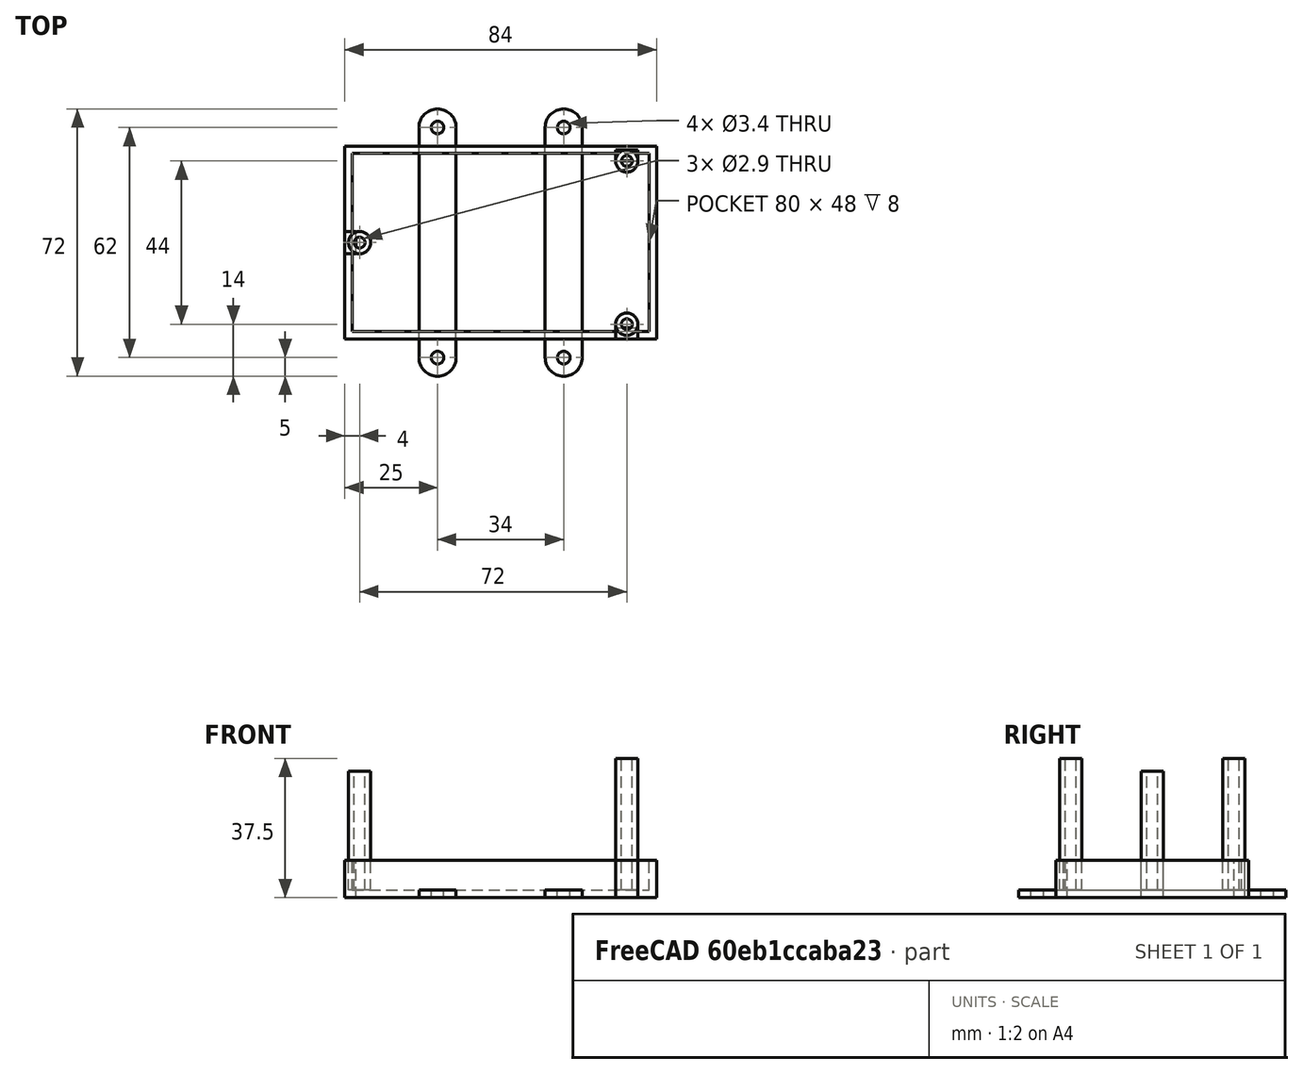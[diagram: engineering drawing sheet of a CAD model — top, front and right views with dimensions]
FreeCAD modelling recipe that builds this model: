
FCSTD DOCUMENT  (FreeCAD 0.18R16093 (Git))
Label: pump_stand
License: All rights reserved
LicenseURL: http://en.wikipedia.org/wiki/All_rights_reserved
objects: Part::Cylinder×14, Part::Box×7, Part::Cut×6, Part::MultiFuse×4, PartDesign::Body×1
note: 32 computed .brp shape members not serialized (recipe doc carries the construction recipe); baked Part::Feature solids carry a one-line shape summary decoded from their .brp

FEATURE [PartDesign::Body] Body
  Origin = -> Origin
FEATURE [Part::Cylinder] Cylinder
  Angle = 360
  AttacherType = Attacher::AttachEngine3D
  Height = 32
  Placement = pos=(4,26,2) rot=(0,0,1;0rad)
  Radius = 3
FEATURE [Part::Box] Box  label="Cube"
  AttacherType = Attacher::AttachEngine3D
  Height = 10
  Length = 84
  Width = 52
FEATURE [Part::Cylinder] Cylinder001
  Angle = 360
  AttacherType = Attacher::AttachEngine3D
  Height = 35.5
  Placement = pos=(76,4,2) rot=(0,0,1;0rad)
  Radius = 3
FEATURE [Part::Cylinder] Cylinder002
  Angle = 360
  AttacherType = Attacher::AttachEngine3D
  Height = 35.5
  Placement = pos=(76,48,2) rot=(0,0,1;0rad)
  Radius = 3
FEATURE [Part::Cylinder] Cylinder003
  Angle = 360
  AttacherType = Attacher::AttachEngine3D
  Height = 35.5
  Placement = pos=(76,4,2) rot=(0,0,1;0rad)
  Radius = 1.45
FEATURE [Part::Cylinder] Cylinder004
  Angle = 360
  AttacherType = Attacher::AttachEngine3D
  Height = 35.5
  Placement = pos=(76,48,2) rot=(0,0,1;0rad)
  Radius = 1.45
FEATURE [Part::Cylinder] Cylinder005
  Angle = 360
  AttacherType = Attacher::AttachEngine3D
  Height = 32
  Placement = pos=(4,26,2) rot=(0,0,1;0rad)
  Radius = 1.45
FEATURE [Part::Cut] Cut
  Base = -> Cylinder
  Tool = -> Cylinder005
FEATURE [Part::Cut] Cut001
  Base = -> Cylinder001
  Tool = -> Cylinder003
FEATURE [Part::Cut] Cut002
  Base = -> Cylinder002
  Tool = -> Cylinder004
FEATURE [Part::Box] Box001  label="Cube001"
  AttacherType = Attacher::AttachEngine3D
  Height = 10
  Length = 80
  Placement = pos=(2,2,2) rot=(0,0,1;0rad)
  Width = 48
FEATURE [Part::Cut] Cut003
  Base = -> Box
  Tool = -> Box001
FEATURE [Part::Box] Box002  label="Cube002"
  AttacherType = Attacher::AttachEngine3D
  Height = 10
  Length = 3
  Placement = pos=(0,23,0) rot=(0,0,1;0rad)
  Width = 6
FEATURE [Part::Box] Box003  label="Cube003"
  AttacherType = Attacher::AttachEngine3D
  Height = 10
  Length = 6
  Placement = pos=(73,0,0) rot=(0,0,1;0rad)
  Width = 3
FEATURE [Part::Box] Box004  label="Cube004"
  AttacherType = Attacher::AttachEngine3D
  Height = 10
  Length = 6
  Placement = pos=(73,48,0) rot=(0,0,1;0rad)
  Width = 3
FEATURE [Part::Box] Box005  label="Cube005"
  AttacherType = Attacher::AttachEngine3D
  Height = 2
  Length = 10
  Placement = pos=(20,-5,0) rot=(0,0,1;0rad)
  Width = 62
FEATURE [Part::Cylinder] Cylinder006
  Angle = 360
  AttacherType = Attacher::AttachEngine3D
  Height = 2
  Placement = pos=(25,-5,0) rot=(0,0,1;0rad)
  Radius = 5
FEATURE [Part::Cylinder] Cylinder007
  Angle = 360
  AttacherType = Attacher::AttachEngine3D
  Height = 2
  Placement = pos=(25,57,0) rot=(0,0,1;0rad)
  Radius = 5
FEATURE [Part::Cylinder] Cylinder008
  Angle = 360
  AttacherType = Attacher::AttachEngine3D
  Height = 2
  Placement = pos=(25,57,0) rot=(0,0,1;0rad)
  Radius = 1.7
FEATURE [Part::MultiFuse] Fusion
  Shapes = -> [Cylinder007,Box005,Cylinder006]
FEATURE [Part::Cylinder] Cylinder009
  Angle = 360
  AttacherType = Attacher::AttachEngine3D
  Height = 2
  Placement = pos=(25,-5,0) rot=(0,0,1;0rad)
  Radius = 1.7
FEATURE [Part::MultiFuse] Fusion001
  Shapes = -> [Cylinder009,Cylinder008]
FEATURE [Part::Cut] Cut004
  Base = -> Fusion
  Tool = -> Fusion001
FEATURE [Part::Cylinder] Cylinder010
  Angle = 360
  AttacherType = Attacher::AttachEngine3D
  Height = 2
  Placement = pos=(25,57,0) rot=(0,0,1;0rad)
  Radius = 1.7
FEATURE [Part::Cylinder] Cylinder011
  Angle = 360
  AttacherType = Attacher::AttachEngine3D
  Height = 2
  Placement = pos=(25,-5,0) rot=(0,0,1;0rad)
  Radius = 1.7
FEATURE [Part::Cylinder] Cylinder012
  Angle = 360
  AttacherType = Attacher::AttachEngine3D
  Height = 2
  Placement = pos=(25,57,0) rot=(0,0,1;0rad)
  Radius = 5
FEATURE [Part::Box] Box006  label="Cube006"
  AttacherType = Attacher::AttachEngine3D
  Height = 2
  Length = 10
  Placement = pos=(20,-5,0) rot=(0,0,1;0rad)
  Width = 62
FEATURE [Part::MultiFuse] Fusion002
  Shapes = -> [Cylinder011,Cylinder010]
FEATURE [Part::Cylinder] Cylinder013
  Angle = 360
  AttacherType = Attacher::AttachEngine3D
  Height = 2
  Placement = pos=(25,-5,0) rot=(0,0,1;0rad)
  Radius = 5
FEATURE [Part::MultiFuse] Fusion003
  Shapes = -> [Cylinder012,Box006,Cylinder013]
FEATURE [Part::Cut] Cut005
  Base = -> Fusion003
  Placement = pos=(34,0,0) rot=(0,0,1;0rad)
  Tool = -> Fusion002
